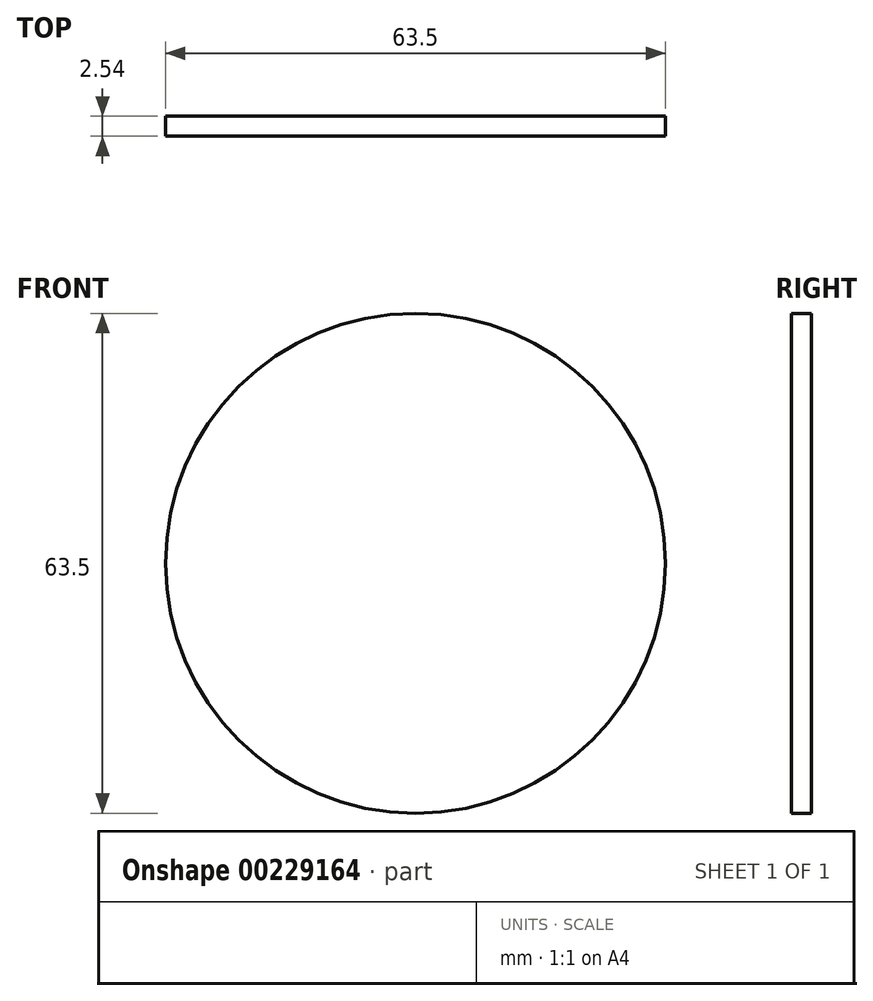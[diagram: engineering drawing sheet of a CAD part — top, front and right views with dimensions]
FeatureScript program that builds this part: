
annotation { "Feature Type Name" : "Feature", "Feature Type Description" : "" }
export const myFeature = defineFeature(function(context is Context, id is Id, definition is map)
    precondition{}
    {
        {
            var Q0;
            Q0=qCreatedBy(makeId("Front.planeOp"),FACE);
            var sketch = newSketch(context, id + "F0", { "sketchPlane" : qUnion([Q0])});
            skCircle(sketch, "E0", {"center": v(0, 0) * mm, "radius": 31.75 * mm});
            skSolve(sketch);
        }
        {
            var Q0;
            Q0=makeQuery(id+"F0.imprint","IMPRINT",FACE,{"disambiguationData":[TD([[makeQuery(id+"F0.imprint","IMPRINT",EDGE,{"derivedFrom":sQuery(id+"F0.wireOp",EDGE,"E0")}),1.0]])]});
            extrude(context, id + "F1", {"entities" : qUnion([Q0]), "depth" : 2.54 * mm});
        }
    });
